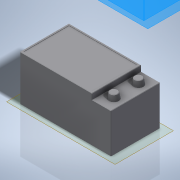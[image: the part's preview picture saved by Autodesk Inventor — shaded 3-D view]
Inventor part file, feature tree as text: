
AUTODESK INVENTOR PART (.ipt)
format: ipt  version: 2022 (Build 260153000, 153)  size: 287,744 bytes
history: native  units: in
note: dims shown in document units (in); Inventor stores cm internally (conversion verified against a paired STEP export)
features: extrude x9, sketch x9, fillet x4
ambient origin geometry x8: Origin, YZ Plane, XZ Plane, XY Plane, X Axis, Y Axis, Z Axis, Center Point
bodies: Body1 (feature_tree)
feature tree (22):
  extrude  "Extrusion5"  Depth=12.3622in
  extrude  "Extrusion6"  Depth=0.3937in
  extrude  "Extrusion7"  Depth=0.7874in
  extrude  "Extrusion8"  Depth=0.3937in TaperAngle=0.0deg
  extrude  "Extrusion9"  Depth=0.7874in
  extrude  "Extrusion10"  Depth=0.3937in
  extrude  "Extrusion11"  Depth=0.9646in
  extrude  "Extrusion12"  TaperAngle=0.0deg  [1 undecoded]
  extrude  "Extrusion13"  Depth=0.1969in TaperAngle=0.0deg
  fillet  "Fillet1"  [1 undecoded]
  fillet  "Fillet2"  [1 undecoded]
  fillet  "Fillet3"  Radius=0.9646in
  fillet  "Fillet4"  [1 undecoded]
  sketch  "Sketch6"  dims[d30=8.937in d31=12.3622in]
  sketch  "Sketch7"  dims[d32=16.4173in d33=0.0in d34=0.3937in]
  sketch  "Sketch8"  dims[d35=0.3937in d36=0.7874in]
  sketch  "Sketch9"  dims[d37=0.7874in d38=0.3937in d39=0.0in]
  sketch  "Sketch10"  dims[d40=0.7874in d41=0.7874in]
  sketch  "Sketch11"  dims[d42=0.3937in d43=0.3937in]
  sketch  "Sketch12"  dims[d44=0.3937in d45=0.0in d46=0.9646in]
  sketch  "Sketch13"  dims[d47=0.9646in d48=0.0in]
  sketch  "Sketch14"  dims[d49=0.0in d50=0.1969in d51=0.0in d52=0.0in d53=0.0in d54=0.9646in d55=0.0in d56=0.0787in d57=0.0in d58=0.0787in d59=0.0in d60=0.0787in d61=0.0in d62=1.9685in d63=1.9685in d64=1.9685in d65=8.937in d66=1.5748in d67=1.5748in d68=90.0deg d69=1.5748in d70=1.9685in d71=1.9685in d72=1.5748in d73=0.0394in d74=0.0in d75=0.3937in d79=0.7874in d80=0.3937in d84=0.3937in d85=0.7874in d86=0.3937in d87=0.3937in d88=0.7874in d89=0.3937in d90=0.1181in d91=0.0in d92=0.0787in d93=0.0787in d94=0.0787in d95=0.0787in]
note: 4 required parameter values undecoded (feature->parameter linkage not recoverable at this tier; creation-order binding heuristic only, values carry confidence <= 0.55)
